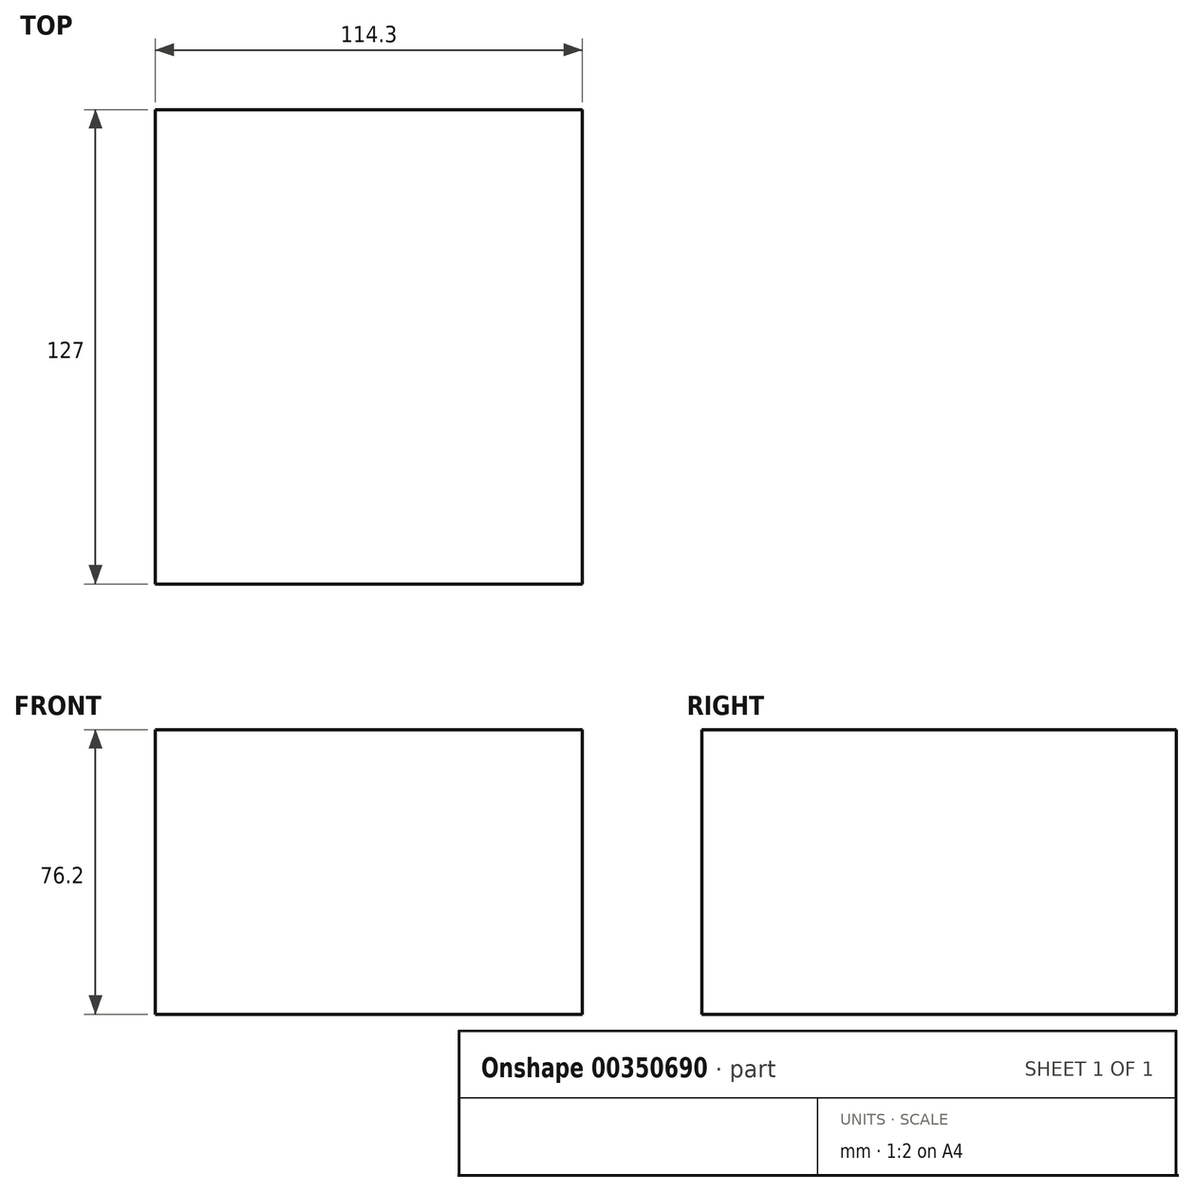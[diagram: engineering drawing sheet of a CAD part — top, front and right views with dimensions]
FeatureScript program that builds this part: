
annotation { "Feature Type Name" : "Feature", "Feature Type Description" : "" }
export const myFeature = defineFeature(function(context is Context, id is Id, definition is map)
    precondition{}
    {
        {
            var Q0;
            Q0=qCreatedBy(makeId("Front.planeOp"),FACE);
            var sketch = newSketch(context, id + "F0", { "sketchPlane" : qUnion([Q0])});
            skLineSegment(sketch, "E0.bottom", {"start": v(-57.15, 38.1) * mm, "end": v(57.15, 38.1) * mm});
            skLineSegment(sketch, "E0.top", {"start": v(-57.15, -38.1) * mm, "end": v(57.15, -38.1) * mm});
            skLineSegment(sketch, "E0.left", {"start": v(-57.15, 38.1) * mm, "end": v(-57.15, -38.1) * mm});
            skLineSegment(sketch, "E0.right", {"start": v(57.15, 38.1) * mm, "end": v(57.15, -38.1) * mm});
            skPoint(sketch, "E0.middle", {"position": v(0, 0) * mm});
            skSolve(sketch);
        }
        {
            var Q0;
            Q0=makeQuery(id+"F0.imprint","IMPRINT",FACE,{"disambiguationData":[TD([[makeQuery(id+"F0.imprint","IMPRINT",EDGE,{"derivedFrom":sQuery(id+"F0.wireOp",EDGE,"E0.bottom")}),-1.0]])]});
            extrude(context, id + "F1", {"entities" : qUnion([Q0]), "oppositeDirection" : true, "depth" : 127 * mm});
        }
    });
